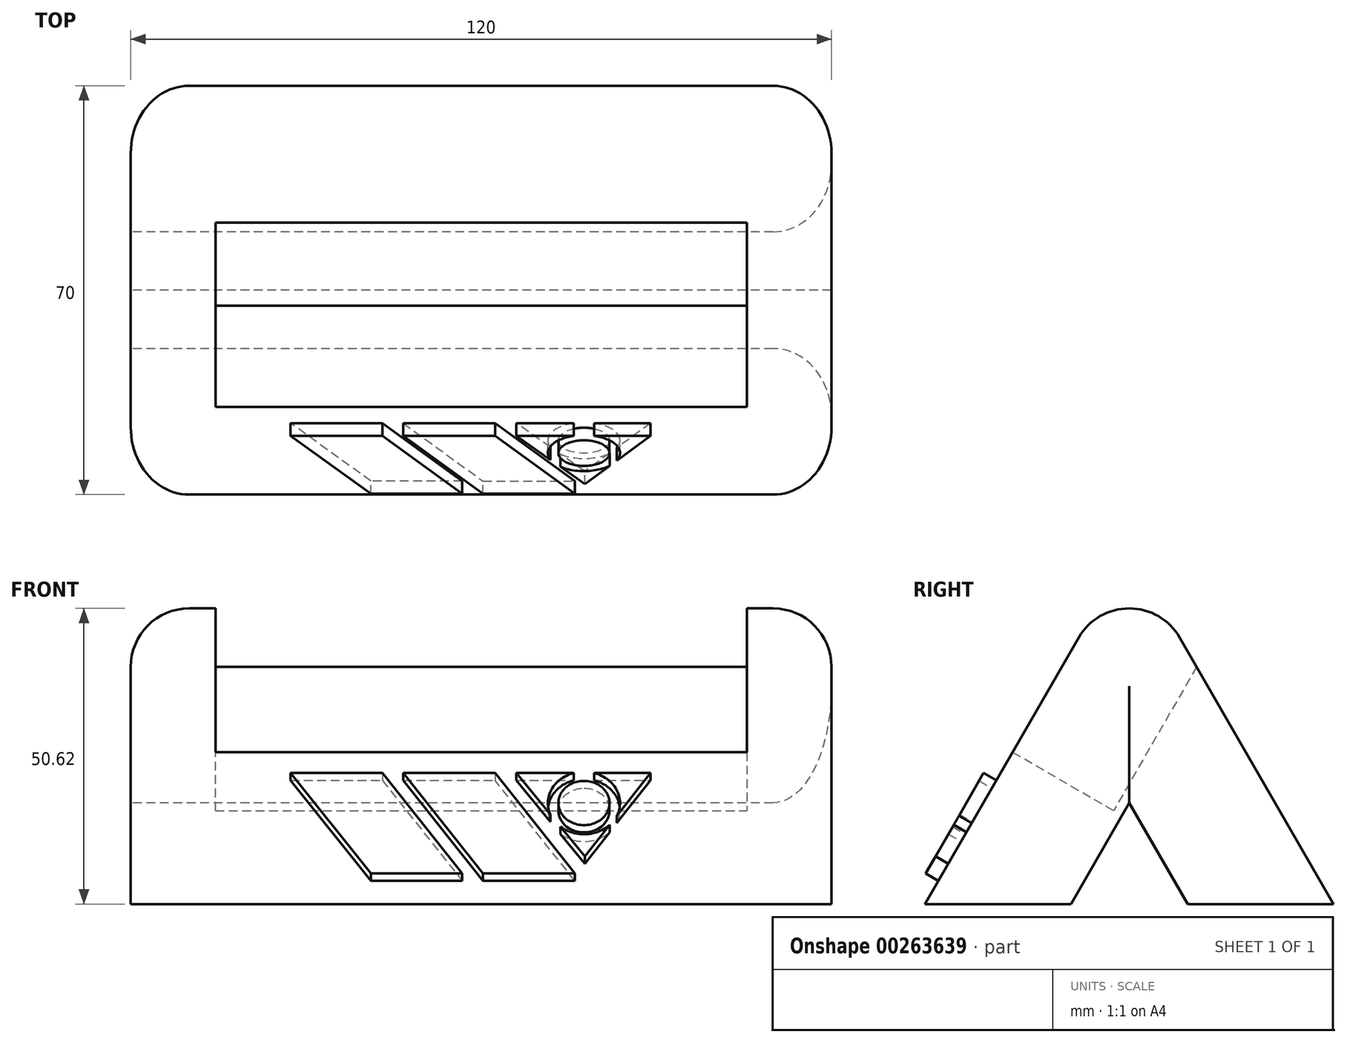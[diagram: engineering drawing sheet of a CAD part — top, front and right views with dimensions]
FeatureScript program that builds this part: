
annotation { "Feature Type Name" : "Feature", "Feature Type Description" : "" }
export const myFeature = defineFeature(function(context is Context, id is Id, definition is map)
    precondition{}
    {
        {
            var Q0;
            Q0=qCreatedBy(makeId("Right.planeOp"),FACE);
            var sketch = newSketch(context, id + "F0", { "sketchPlane" : qUnion([Q0])});
            skLineSegment(sketch, "E0", {"start": v(0, 60.62) * mm, "end": v(-35, 0) * mm});
            skLineSegment(sketch, "E1", {"start": v(-35, 0) * mm, "end": v(35, 0) * mm});
            skLineSegment(sketch, "E2", {"start": v(35, 0) * mm, "end": v(0, 60.62) * mm});
            skSolve(sketch);
        }
        {
            var Q0;
            Q0=makeQuery(id+"F0.imprint","IMPRINT",FACE,{"disambiguationData":[TD([[makeQuery(id+"F0.imprint","IMPRINT",EDGE,{"derivedFrom":sQuery(id+"F0.wireOp",EDGE,"E0")}),1.0]])]});
            extrude(context, id + "F1", {"entities" : qUnion([Q0]), "endBound" : BoundingType.SYMMETRIC, "depth" : 120 * mm});
        }
        {
            var Q0;
            Q0=makeQuery(id+"F1.opExtrude","SWEPT_FACE",FACE,{"disambiguationData":[OSD([sQuery(id+"F0.wireOp",EDGE,"E0")])]});
            var sketch = newSketch(context, id + "F2", { "sketchPlane" : qUnion([Q0])});
            skLineSegment(sketch, "E3.bottom", {"start": v(-45.5, 52.5) * mm, "end": v(45.5, 52.5) * mm});
            skLineSegment(sketch, "E3.top", {"start": v(-45.5, 12.5) * mm, "end": v(45.5, 12.5) * mm});
            skLineSegment(sketch, "E3.left", {"start": v(-45.5, 52.5) * mm, "end": v(-45.5, 12.5) * mm});
            skLineSegment(sketch, "E3.right", {"start": v(45.5, 52.5) * mm, "end": v(45.5, 12.5) * mm});
            skSolve(sketch);
        }
        {
            var Q0;
            Q0=makeQuery(id+"F2.imprint","IMPRINT",FACE,{"disambiguationData":[TD([[makeQuery(id+"F2.imprint","IMPRINT",EDGE,{"derivedFrom":sQuery(id+"F2.wireOp",EDGE,"E3.bottom")}),1.0]])]});
            extrude(context, id + "F3", {"entities" : qUnion([Q0]), "operationType" : NewBodyOperationType.REMOVE, "oppositeDirection" : true, "depth" : 20 * mm});
        }
        {
            var Q0;
            Q0=makeQuery(id+"F1.opExtrude","SWEPT_FACE",FACE,{"disambiguationData":[OSD([sQuery(id+"F0.wireOp",EDGE,"E0")])]});
            var sketch = newSketch(context, id + "F4", { "sketchPlane" : qUnion([Q0])});
            skLineSegment(sketch, "E4", {"start": v(-32.64, 6.96) * mm, "end": v(-16.91, 6.96) * mm});
            skLineSegment(sketch, "E5", {"start": v(-16.91, 6.96) * mm, "end": v(-3.23, -12.92) * mm});
            skLineSegment(sketch, "E6", {"start": v(-3.23, -12.92) * mm, "end": v(-18.86, -12.92) * mm});
            skLineSegment(sketch, "E7", {"start": v(-18.86, -12.92) * mm, "end": v(-32.64, 6.96) * mm});
            skLineSegment(sketch, "E8", {"start": v(-13.35, 6.96) * mm, "end": v(2.38, 6.96) * mm});
            skLineSegment(sketch, "E9", {"start": v(0.33, -12.92) * mm, "end": v(16.06, -12.92) * mm});
            skLineSegment(sketch, "E10", {"start": v(16.06, -12.92) * mm, "end": v(2.38, 6.96) * mm});
            skLineSegment(sketch, "E11", {"start": v(-13.35, 6.96) * mm, "end": v(0.33, -12.92) * mm});
            skLineSegment(sketch, "E12", {"start": v(6.03, 6.96) * mm, "end": v(15.9, 6.96) * mm});
            skLineSegment(sketch, "E13", {"start": v(29.03, 6.96) * mm, "end": v(23.25, -1.5) * mm});
            skLineSegment(sketch, "E14", {"start": v(17.76, -9.53) * mm, "end": v(13.57, -3.64) * mm});
            skCircle(sketch, "E15", {"center": v(17.62, 1.03) * mm, "radius": 4.38 * mm});
            skArc(sketch, "E16", {"start": v(15.9, 6.96) * mm, "mid": v(12.07, 3.74) * mm, "end": v(11.88, -1.26) * mm});
            skLineSegment(sketch, "E17.trimOffspring", {"start": v(19.34, 6.96) * mm, "end": v(29.03, 6.96) * mm});
            skPoint(sketch, "E18.orphan", {"position": v(17.53, 6.96) * mm});
            skArc(sketch, "E19.trimOffspring", {"start": v(23.25, -1.5) * mm, "mid": v(23.22, 3.62) * mm, "end": v(19.34, 6.96) * mm});
            skLineSegment(sketch, "E20.trimOffspring", {"start": v(22.02, -3.3) * mm, "end": v(17.76, -9.53) * mm});
            skLineSegment(sketch, "E21.trimOffspring", {"start": v(11.88, -1.26) * mm, "end": v(6.03, 6.96) * mm});
            skArc(sketch, "E22.trimOffspring", {"start": v(13.57, -3.64) * mm, "mid": v(17.86, -5.14) * mm, "end": v(22.02, -3.3) * mm});
            skSolve(sketch);
        }
        {
            var Q0;
            Q0=makeQuery(id+"F4.imprint","IMPRINT",FACE,{"disambiguationData":[TD([[makeQuery(id+"F4.imprint","IMPRINT",EDGE,{"derivedFrom":sQuery(id+"F4.wireOp",EDGE,"E4")}),-1.0]])]});
            var Q1;
            Q1=makeQuery(id+"F4.imprint","IMPRINT",FACE,{"disambiguationData":[TD([[makeQuery(id+"F4.imprint","IMPRINT",EDGE,{"derivedFrom":sQuery(id+"F4.wireOp",EDGE,"E8")}),-1.0]])]});
            var Q2;
            Q2=makeQuery(id+"F4.imprint","IMPRINT",FACE,{"disambiguationData":[TD([[makeQuery(id+"F4.imprint","IMPRINT",EDGE,{"derivedFrom":sQuery(id+"F4.wireOp",EDGE,"E12")}),-1.0]])]});
            var Q3;
            Q3=makeQuery(id+"F4.imprint","IMPRINT",FACE,{"disambiguationData":[TD([[makeQuery(id+"F4.imprint","IMPRINT",EDGE,{"derivedFrom":sQuery(id+"F4.wireOp",EDGE,"E15")}),1.0]])]});
            var Q4;
            Q4=makeQuery(id+"F4.imprint","IMPRINT",FACE,{"disambiguationData":[TD([[makeQuery(id+"F4.imprint","IMPRINT",EDGE,{"derivedFrom":sQuery(id+"F4.wireOp",EDGE,"E13")}),-1.0]])]});
            var Q5;
            Q5=makeQuery(id+"F4.imprint","IMPRINT",FACE,{"disambiguationData":[TD([[makeQuery(id+"F4.imprint","IMPRINT",EDGE,{"derivedFrom":sQuery(id+"F4.wireOp",EDGE,"E14")}),-1.0]])]});
            extrude(context, id + "F5", {"entities" : qUnion([Q0, Q1, Q2, Q3, Q4, Q5]), "operationType" : NewBodyOperationType.ADD, "depth" : 2.5 * mm});
        }
        {
            var Q0;
            Q0=makeQuery(id+"F1.opExtrude","CAP_FACE",FACE,{"disambiguationData":[OSD([sQuery(id+"F0.wireOp",EDGE,"E0"),sQuery(id+"F0.wireOp",EDGE,"E1"),sQuery(id+"F0.wireOp",EDGE,"E2")])],"isStart":true});
            var sketch = newSketch(context, id + "F6", { "sketchPlane" : qUnion([Q0])});
            skLineSegment(sketch, "E23", {"start": v(0, 17.32) * mm, "end": v(-10, 0) * mm});
            skLineSegment(sketch, "E24", {"start": v(-10, 0) * mm, "end": v(10, 0) * mm});
            skLineSegment(sketch, "E25", {"start": v(10, 0) * mm, "end": v(0, 17.32) * mm});
            skSolve(sketch);
        }
        {
            var Q0;
            Q0=makeQuery(id+"F6.imprint","IMPRINT",FACE,{"disambiguationData":[TD([[makeQuery(id+"F6.imprint","IMPRINT",EDGE,{"derivedFrom":sQuery(id+"F6.wireOp",EDGE,"E23")}),1.0]])]});
            extrude(context, id + "F7", {"entities" : qUnion([Q0]), "operationType" : NewBodyOperationType.REMOVE, "endBound" : BoundingType.THROUGH_ALL, "oppositeDirection" : true, "depth" : 25 * mm});
        }
        {
            var Q0;
            {var subQ0=sQuery(id+"F0.wireOp",EDGE,"E0");var subQ1=sQuery(id+"F0.wireOp",EDGE,"E2");Q0=makeQuery(id+"F3.boolean.opBoolean","SPLIT",EDGE,{"disambiguationData":[TD([makeQuery(id+"F3.opExtrude","SWEPT_FACE",FACE,{"disambiguationData":[OSD([sQuery(id+"F2.wireOp",EDGE,"E3.right")])]})])],"derivedFrom":makeQuery(id+"F1.opExtrude","SWEPT_EDGE",EDGE,{"disambiguationData":[OSD([subQ0,subQ1])]})});}
            var Q1;
            {var subQ0=sQuery(id+"F0.wireOp",EDGE,"E0");var subQ1=sQuery(id+"F0.wireOp",EDGE,"E2");Q1=makeQuery(id+"F3.boolean.opBoolean","SPLIT",EDGE,{"disambiguationData":[TD([makeQuery(id+"F3.opExtrude","SWEPT_FACE",FACE,{"disambiguationData":[OSD([sQuery(id+"F2.wireOp",EDGE,"E3.left")])]})])],"derivedFrom":makeQuery(id+"F1.opExtrude","SWEPT_EDGE",EDGE,{"disambiguationData":[OSD([subQ0,subQ1])]})});}
            var Q2;
            Q2=makeQuery(id+"F1.opExtrude","CAP_EDGE",EDGE,{"disambiguationData":[OSD([sQuery(id+"F0.wireOp",EDGE,"E0")])],"isStart":true});
            var Q3;
            Q3=makeQuery(id+"F1.opExtrude","CAP_EDGE",EDGE,{"disambiguationData":[OSD([sQuery(id+"F0.wireOp",EDGE,"E2")])],"isStart":false});
            var Q4;
            Q4=makeQuery(id+"F1.opExtrude","CAP_EDGE",EDGE,{"disambiguationData":[OSD([sQuery(id+"F0.wireOp",EDGE,"E0")])],"isStart":false});
            var Q5;
            Q5=makeQuery(id+"F1.opExtrude","CAP_EDGE",EDGE,{"disambiguationData":[OSD([sQuery(id+"F0.wireOp",EDGE,"E2")])],"isStart":true});
            var Q6;
            Q6=makeQuery(id+"F7.boolean.opBoolean","COPY",EDGE,{"derivedFrom":makeQuery(id+"F7.opExtrude","CAP_EDGE",EDGE,{"disambiguationData":[OSD([sQuery(id+"F6.wireOp",EDGE,"E25")])],"isStart":true})});
            var Q7;
            Q7=makeQuery(id+"F7.boolean.opBoolean","COPY",EDGE,{"derivedFrom":makeQuery(id+"F7.opExtrude","CAP_EDGE",EDGE,{"disambiguationData":[OSD([sQuery(id+"F6.wireOp",EDGE,"E23")])],"isStart":true})});
            var Q8;
            Q8=makeQuery(id+"F7.boolean.opBoolean","INTERSECT",EDGE,{"derivedFrom":[makeQuery(id+"F1.opExtrude","CAP_FACE",FACE,{"disambiguationData":[OSD([sQuery(id+"F0.wireOp",EDGE,"E0"),sQuery(id+"F0.wireOp",EDGE,"E1"),sQuery(id+"F0.wireOp",EDGE,"E2")])],"isStart":false}),makeQuery(id+"F7.opExtrude","SWEPT_FACE",FACE,{"disambiguationData":[OSD([sQuery(id+"F6.wireOp",EDGE,"E25")])]})]});
            var Q9;
            Q9=makeQuery(id+"F7.boolean.opBoolean","INTERSECT",EDGE,{"derivedFrom":[makeQuery(id+"F1.opExtrude","CAP_FACE",FACE,{"disambiguationData":[OSD([sQuery(id+"F0.wireOp",EDGE,"E0"),sQuery(id+"F0.wireOp",EDGE,"E1"),sQuery(id+"F0.wireOp",EDGE,"E2")])],"isStart":false}),makeQuery(id+"F7.opExtrude","SWEPT_FACE",FACE,{"disambiguationData":[OSD([sQuery(id+"F6.wireOp",EDGE,"E23")])]})]});
            fillet(context, id + "F8", {"entities" : qUnion([Q0, Q1, Q2, Q3, Q4, Q5, Q6, Q7, Q8, Q9]), "radius" : 10 * mm, "tangentPropagation" : true, "allowEdgeOverflow" : false});
        }
    });
